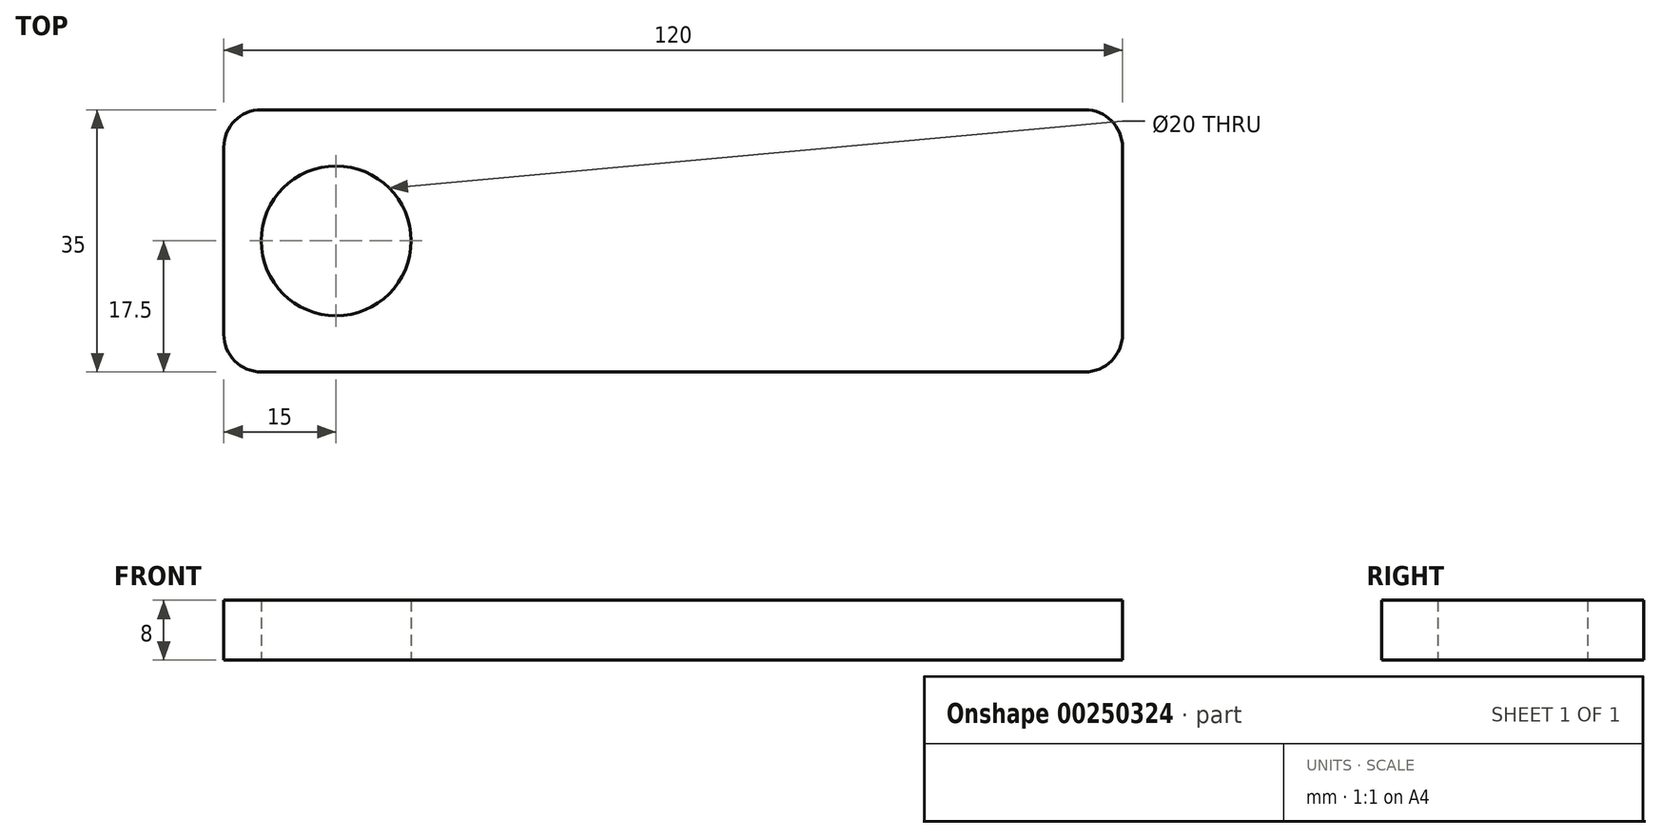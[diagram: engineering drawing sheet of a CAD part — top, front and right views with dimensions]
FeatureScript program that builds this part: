
annotation { "Feature Type Name" : "Feature", "Feature Type Description" : "" }
export const myFeature = defineFeature(function(context is Context, id is Id, definition is map)
    precondition{}
    {
        {
            var Q0;
            Q0=qCreatedBy(makeId("Top.planeOp"),FACE);
            var sketch = newSketch(context, id + "F0", { "sketchPlane" : qUnion([Q0])});
            skLineSegment(sketch, "E0.bottom", {"start": v(-60, -17.5) * mm, "end": v(60, -17.5) * mm});
            skLineSegment(sketch, "E0.top", {"start": v(-60, 17.5) * mm, "end": v(60, 17.5) * mm});
            skLineSegment(sketch, "E0.left", {"start": v(-60, -17.5) * mm, "end": v(-60, 17.5) * mm});
            skLineSegment(sketch, "E0.right", {"start": v(60, -17.5) * mm, "end": v(60, 17.5) * mm});
            skPoint(sketch, "E0.middle", {"position": v(0, 0) * mm});
            skCircle(sketch, "E1", {"center": v(-45, 0) * mm, "radius": 10 * mm});
            skSolve(sketch);
        }
        {
            var Q0;
            Q0=makeQuery(id+"F0.imprint","IMPRINT",FACE,{"disambiguationData":[TD([[makeQuery(id+"F0.imprint","IMPRINT",EDGE,{"derivedFrom":sQuery(id+"F0.wireOp",EDGE,"E0.bottom")}),1.0]])]});
            extrude(context, id + "F1", {"entities" : qUnion([Q0]), "depth" : 5 * mm});
        }
        {
            var Q0;
            Q0=makeQuery(id+"F1.opExtrude","SWEPT_EDGE",EDGE,{"disambiguationData":[OSD([sQuery(id+"F0.wireOp",EDGE,"E0.bottom"),sQuery(id+"F0.wireOp",EDGE,"E0.left")])]});
            var Q1;
            Q1=makeQuery(id+"F1.opExtrude","SWEPT_EDGE",EDGE,{"disambiguationData":[OSD([sQuery(id+"F0.wireOp",EDGE,"E0.top"),sQuery(id+"F0.wireOp",EDGE,"E0.left")])]});
            var Q2;
            Q2=makeQuery(id+"F1.opExtrude","SWEPT_EDGE",EDGE,{"disambiguationData":[OSD([sQuery(id+"F0.wireOp",EDGE,"E0.top"),sQuery(id+"F0.wireOp",EDGE,"E0.right")])]});
            var Q3;
            Q3=makeQuery(id+"F1.opExtrude","SWEPT_EDGE",EDGE,{"disambiguationData":[OSD([sQuery(id+"F0.wireOp",EDGE,"E0.bottom"),sQuery(id+"F0.wireOp",EDGE,"E0.right")])]});
            fillet(context, id + "F2", {"entities" : qUnion([Q0, Q1, Q2, Q3]), "radius" : 5 * mm, "tangentPropagation" : true, "allowEdgeOverflow" : false});
        }
        {
            var Q0;
            Q0=makeQuery(id+"F1.opExtrude","CAP_FACE",FACE,{"disambiguationData":[OSD([sQuery(id+"F0.wireOp",EDGE,"E0.bottom"),sQuery(id+"F0.wireOp",EDGE,"E0.top"),sQuery(id+"F0.wireOp",EDGE,"E0.left"),sQuery(id+"F0.wireOp",EDGE,"E0.right"),sQuery(id+"F0.wireOp",EDGE,"E1")])],"isStart":false});
            extrude(context, id + "F3", {"entities" : qUnion([Q0]), "operationType" : NewBodyOperationType.ADD, "depth" : 3 * mm});
        }
    });
